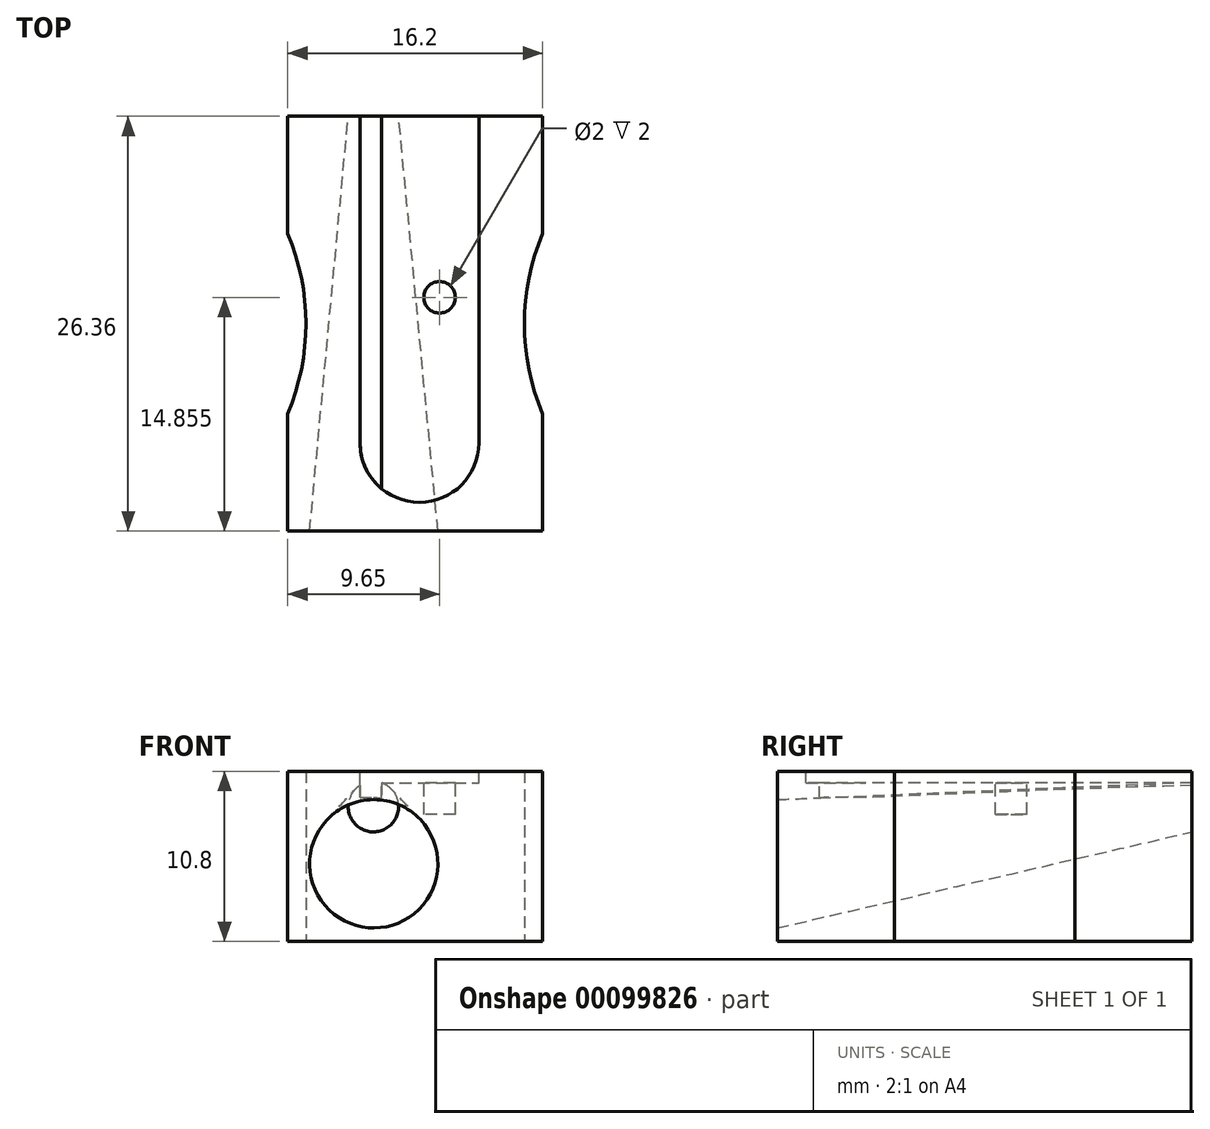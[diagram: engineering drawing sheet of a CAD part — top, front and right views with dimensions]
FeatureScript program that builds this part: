
annotation { "Feature Type Name" : "Feature", "Feature Type Description" : "" }
export const myFeature = defineFeature(function(context is Context, id is Id, definition is map)
    precondition{}
    {
        {
            var Q0;
            Q0=qCreatedBy(makeId("Top.planeOp"),FACE);
            var sketch = newSketch(context, id + "F0", { "sketchPlane" : qUnion([Q0])});
            skLineSegment(sketch, "E0.bottom", {"start": v(-8.1, 13.17) * mm, "end": v(0, 13.17) * mm});
            skLineSegment(sketch, "E0.top", {"start": v(-8.1, -13.17) * mm, "end": v(0, -13.17) * mm});
            skLineSegment(sketch, "E0.left", {"start": v(-8.1, 13.18) * mm, "end": v(-8.1, 5.73) * mm});
            skLineSegment(sketch, "E1", {"start": v(-6.94, 0) * mm, "end": v(0, 0) * mm});
            skArc(sketch, "E2", {"start": v(-8.1, -5.73) * mm, "mid": v(-6.94, 0) * mm, "end": v(-8.1, 5.73) * mm});
            skLineSegment(sketch, "E3.trimOffspring", {"start": v(-8.1, -5.73) * mm, "end": v(-8.1, -13.18) * mm});
            skPoint(sketch, "E4.orphan", {"position": v(-8.1, 0) * mm});
            skLineSegment(sketch, "E5", {"start": v(0, 13.17) * mm, "end": v(0, -13.17) * mm});
            skPoint(sketch, "E6.orphan", {"position": v(8.56, 13.17) * mm});
            skPoint(sketch, "E0.right.start.orphan", {"position": v(8.56, 0) * mm});
            skPoint(sketch, "E7.orphan", {"position": v(8.56, -13.17) * mm});
            skSolve(sketch);
        }
        {
            var Q0;
            Q0 = qSketchRegion(id + "F0", true);
            extrude(context, id + "F1", {"entities" : qUnion([Q0]), "depth" : 10.8 * mm});
        }
        {
            var Q0;
            Q0=makeQuery(id+"F1.opExtrude","SWEPT_BODY",BODY,{"disambiguationData":[OSD([sQuery(id+"F0.wireOp",EDGE,"E0.bottom"),sQuery(id+"F0.wireOp",EDGE,"E0.top"),sQuery(id+"F0.wireOp",EDGE,"E0.left"),sQuery(id+"F0.wireOp",EDGE,"E2"),sQuery(id+"F0.wireOp",EDGE,"E3.trimOffspring"),sQuery(id+"F0.wireOp",EDGE,"E5")])]});
            var Q1;
            Q1=qCreatedBy(makeId("Right.planeOp"),FACE);
            mirror(context, id + "F2", {"operationType" : NewBodyOperationType.ADD, "entities" : qUnion([Q0]), "mirrorPlane" : qUnion([Q1])});
        }
        {
            var Q0;
            {var subQ0=makeQuery(id+"F1.opExtrude","CAP_FACE",FACE,{"disambiguationData":[OSD([sQuery(id+"F0.wireOp",EDGE,"E0.bottom"),sQuery(id+"F0.wireOp",EDGE,"E0.top"),sQuery(id+"F0.wireOp",EDGE,"E0.left"),sQuery(id+"F0.wireOp",EDGE,"E2"),sQuery(id+"F0.wireOp",EDGE,"E3.trimOffspring"),sQuery(id+"F0.wireOp",EDGE,"E5")])],"isStart":false});Q0=makeQuery(id+"F2.boolean.opBoolean","MERGE",FACE,{"derivedFrom":[subQ0,makeQuery(id+"F2.opPattern","COPY",FACE,{"derivedFrom":subQ0,"instanceName":"1"})]});}
            var sketch = newSketch(context, id + "F3", { "sketchPlane" : qUnion([Q0])});
            skLineSegment(sketch, "E8", {"start": v(-3.5, 13.17) * mm, "end": v(-3.5, -7.58) * mm});
            skLineSegment(sketch, "E9", {"start": v(4.05, 13.17) * mm, "end": v(4.05, -7.58) * mm});
            skArc(sketch, "E10", {"start": v(-3.5, -7.58) * mm, "mid": v(0.28, -11.35) * mm, "end": v(4.05, -7.58) * mm});
            skSolve(sketch);
        }
        {
            var Q0;
            {var subQ0=makeQuery(id+"F1.opExtrude","SWEPT_FACE",FACE,{"disambiguationData":[OSD([sQuery(id+"F0.wireOp",EDGE,"E0.top")])]});Q0=makeQuery(id+"F2.boolean.opBoolean","MERGE",FACE,{"derivedFrom":[subQ0,makeQuery(id+"F2.opPattern","COPY",FACE,{"derivedFrom":subQ0,"instanceName":"1"})]});}
            var sketch = newSketch(context, id + "F4", { "sketchPlane" : qUnion([Q0])});
            skCircle(sketch, "E11", {"center": v(-2.63, 4.92) * mm, "radius": 4.08 * mm});
            skSolve(sketch);
        }
        {
            var Q0;
            {var subQ0=makeQuery(id+"F1.opExtrude","SWEPT_FACE",FACE,{"disambiguationData":[OSD([sQuery(id+"F0.wireOp",EDGE,"E0.bottom")])]});Q0=makeQuery(id+"F2.boolean.opBoolean","MERGE",FACE,{"derivedFrom":[subQ0,makeQuery(id+"F2.opPattern","COPY",FACE,{"derivedFrom":subQ0,"instanceName":"1"})]});}
            var sketch = newSketch(context, id + "F5", { "sketchPlane" : qUnion([Q0])});
            skCircle(sketch, "E12", {"center": v(2.65, 8.55) * mm, "radius": 1.6 * mm});
            skSolve(sketch);
        }
        {
            var Q1;
            Q1=makeQuery(id+"F5.imprint","IMPRINT",FACE,{"disambiguationData":[TD([[makeQuery(id+"F5.imprint","IMPRINT",EDGE,{"derivedFrom":sQuery(id+"F5.wireOp",EDGE,"E12")}),1.0]])]});
            var Q2;
            Q2=makeQuery(id+"F4.imprint","IMPRINT",FACE,{"disambiguationData":[TD([[makeQuery(id+"F4.imprint","IMPRINT",EDGE,{"derivedFrom":sQuery(id+"F4.wireOp",EDGE,"E11")}),1.0]])]});
            loft(context, id + "F6", {"operationType" : NewBodyOperationType.REMOVE, "sheetProfilesArray" : [{ "sheetProfileEntities" : qUnion([Q1]) }, { "sheetProfileEntities" : qUnion([Q2]) }]});
        }
        {
            var Q0;
            {var subQ0=sQuery(id+"F3.wireOp",EDGE,"E8");Q0=makeQuery(id+"F3.imprint","IMPRINT",FACE,{"disambiguationData":[TD([[makeQuery(id+"F3.imprint","IMPRINT",EDGE,{"derivedFrom":subQ0}),1.0]])]});}
            extrude(context, id + "F7", {"entities" : qUnion([Q0]), "operationType" : NewBodyOperationType.REMOVE, "oppositeDirection" : true, "depth" : 0.74 * mm});
        }
        {
            var Q0;
            Q0=makeQuery(id+"F7.boolean.opBoolean","COPY",FACE,{"derivedFrom":makeQuery(id+"F7.opExtrude","CAP_FACE",FACE,{"disambiguationData":[OSD([sQuery(id+"F0.wireOp",EDGE,"E0.bottom"),sQuery(id+"F3.wireOp",EDGE,"E8"),sQuery(id+"F3.wireOp",EDGE,"E9"),sQuery(id+"F3.wireOp",EDGE,"E10")])],"isStart":false})});
            var sketch = newSketch(context, id + "F8", { "sketchPlane" : qUnion([Q0])});
            skLineSegment(sketch, "E13", {"start": v(-2.13, 13.17) * mm, "end": v(-2.13, -10.48) * mm});
            skLineSegment(sketch, "E14", {"start": v(-2.13, 13.17) * mm, "end": v(-3.5, 13.17) * mm});
            skLineSegment(sketch, "E15", {"start": v(-3.5, 13.17) * mm, "end": v(-3.5, -7.58) * mm});
            skArc(sketch, "E16", {"start": v(-3.5, -7.58) * mm, "mid": v(-3.14, -9.18) * mm, "end": v(-2.13, -10.48) * mm});
            skSolve(sketch);
        }
        {
            var Q0;
            {var subQ0=sQuery(id+"F8.wireOp",EDGE,"E13");Q0=makeQuery(id+"F8.imprint","IMPRINT",FACE,{"disambiguationData":[TD([[makeQuery(id+"F8.imprint","IMPRINT",EDGE,{"derivedFrom":subQ0}),1.0]])]});}
            var sketch = newSketch(context, id + "F9", { "sketchPlane" : qUnion([Q0])});
            skCircle(sketch, "E17", {"center": v(1.55, 1.67) * mm, "radius": 1 * mm});
            skSolve(sketch);
        }
        {
            var Q0;
            Q0 = qSketchRegion(id + "F9", true);
            extrude(context, id + "F10", {"entities" : qUnion([Q0]), "operationType" : NewBodyOperationType.REMOVE, "oppositeDirection" : true, "depth" : 2 * mm});
        }
        {
            var Q0;
            Q0 = qSketchRegion(id + "F8", true);
            extrude(context, id + "F11", {"entities" : qUnion([Q0]), "operationType" : NewBodyOperationType.REMOVE, "oppositeDirection" : true, "depth" : 1.5 * mm});
        }
    });
